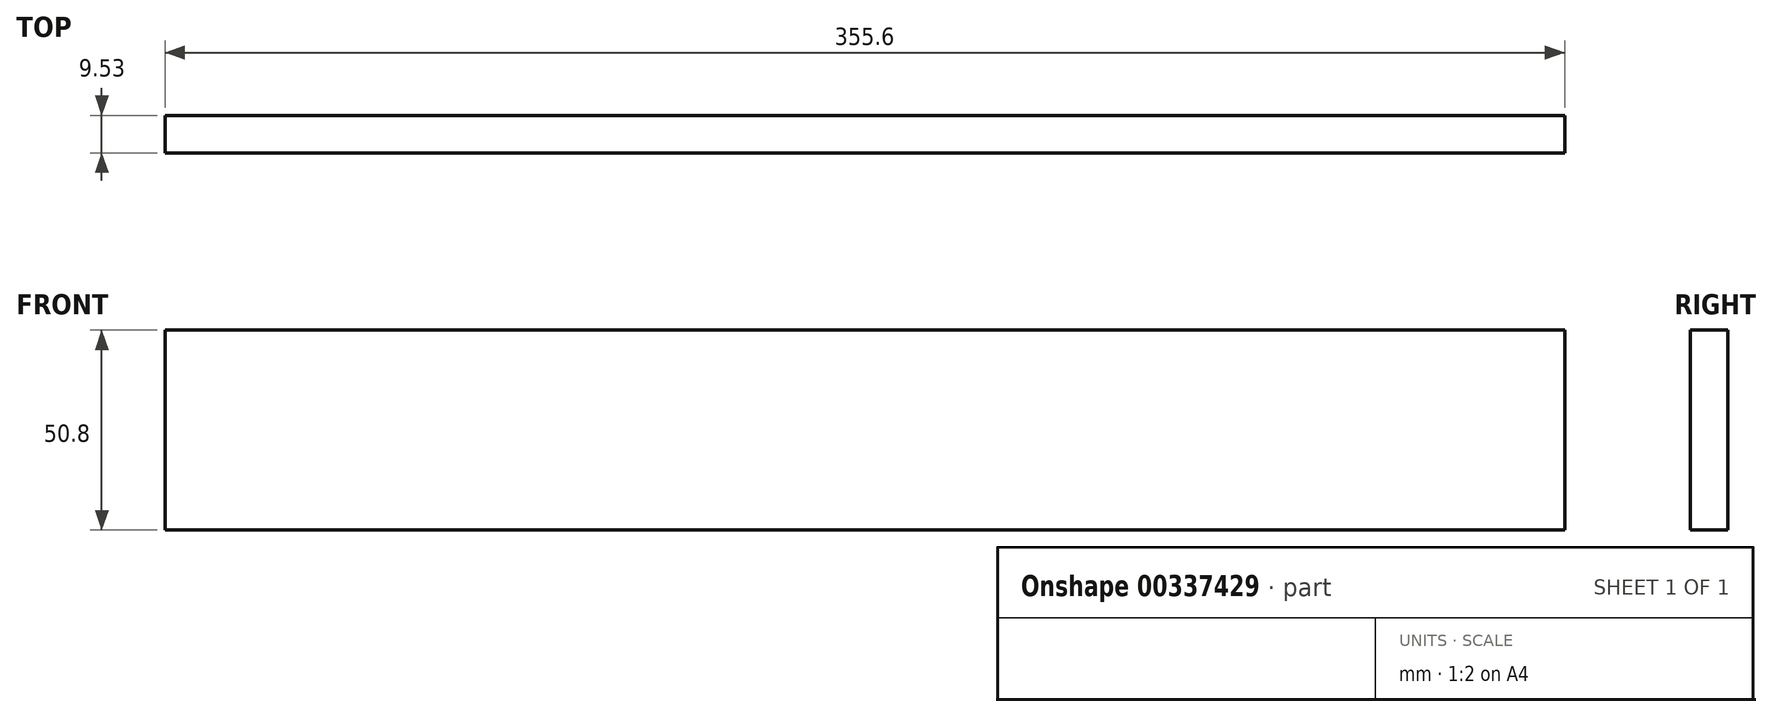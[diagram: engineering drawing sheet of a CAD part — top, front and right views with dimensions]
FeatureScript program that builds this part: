
annotation { "Feature Type Name" : "Feature", "Feature Type Description" : "" }
export const myFeature = defineFeature(function(context is Context, id is Id, definition is map)
    precondition{}
    {
        {
            var Q0;
            Q0=qCreatedBy(makeId("Front.planeOp"),FACE);
            var sketch = newSketch(context, id + "F0", { "sketchPlane" : qUnion([Q0])});
            skLineSegment(sketch, "E0.bottom", {"start": v(177.8, 25.4) * mm, "end": v(-177.8, 25.4) * mm});
            skLineSegment(sketch, "E0.top", {"start": v(177.8, -25.4) * mm, "end": v(-177.8, -25.4) * mm});
            skLineSegment(sketch, "E0.left", {"start": v(177.8, 25.4) * mm, "end": v(177.8, -25.4) * mm});
            skLineSegment(sketch, "E0.right", {"start": v(-177.8, 25.4) * mm, "end": v(-177.8, -25.4) * mm});
            skPoint(sketch, "E0.middle", {"position": v(0, 0) * mm});
            skSolve(sketch);
        }
        {
            var Q0;
            Q0 = qSketchRegion(id + "F0", true);
            extrude(context, id + "F1", {"entities" : qUnion([Q0]), "depth" : 9.52 * mm});
        }
    });
